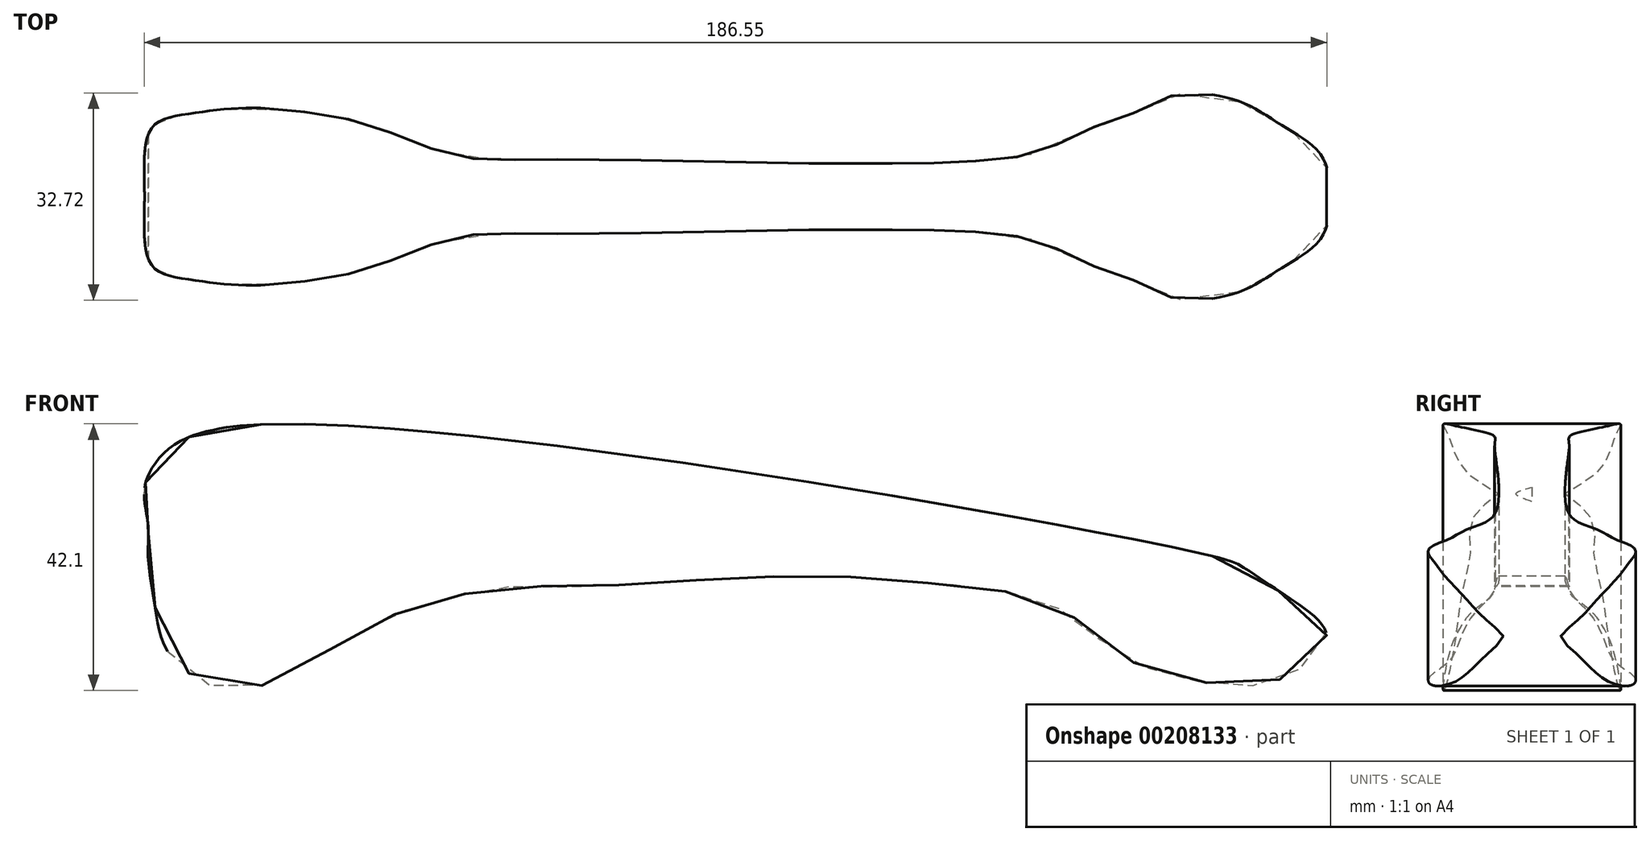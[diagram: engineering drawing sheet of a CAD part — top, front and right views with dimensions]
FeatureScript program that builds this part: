
annotation { "Feature Type Name" : "Feature", "Feature Type Description" : "" }
export const myFeature = defineFeature(function(context is Context, id is Id, definition is map)
    precondition{}
    {
        {
            var Q0;
            Q0=qCreatedBy(makeId("Front.planeOp"),FACE);
            var sketch = newSketch(context, id + "F0", { "sketchPlane" : qUnion([Q0])});
            skFitSpline(sketch, "E0", {"points": [v(-91, 27.57) * mm, v(-74.43, 33.6) * mm, v(75.64, 12.8) * mm, v(81.06, 10.7) * mm, v(88.3, 5.88) * mm, v(93.72, 0) * mm, v(88.6, -5.58) * mm, v(80.46, -7.68) * mm, v(68.7, -5.88) * mm, v(60.27, -2.26) * mm, v(53.34, 3.47) * mm, v(40.68, 7.68) * mm, v(30.14, 8.59) * mm, v(19.29, 9.5) * mm, v(3.31, 9.5) * mm, v(-7.53, 8.9) * mm, v(-26.22, 7.99) * mm, v(-35.56, 7.99) * mm, v(-44.9, 6.18) * mm, v(-53.64, 3.47) * mm, v(-59.97, 0) * mm, v(-68.7, -4.67) * mm, v(-74.43, -7.68) * mm, v(-81.37, -7.99) * mm, v(-88.9, -2.56) * mm, v(-91, 4.07) * mm, v(-92.21, 12.8) * mm, v(-92.21, 17.63) * mm, v(-92.82, 23.05) * mm, v(-91, 27.57) * mm]});
            skLineSegment(sketch, "E1", {"start": v(-74.43, 33.6) * mm, "end": v(75.64, 12.8) * mm});
            skSolve(sketch);
        }
        {
            var Q0;
            Q0=qCreatedBy(makeId("Top.planeOp"),FACE);
            var sketch = newSketch(context, id + "F1", { "sketchPlane" : qUnion([Q0])});
            skFitSpline(sketch, "E2", {"points": [v(-92.75, 0) * mm, v(-92.75, 6.78) * mm, v(-91.25, 11.3) * mm, v(-85.52, 13.1) * mm, v(-76.18, 14.01) * mm, v(-65.63, 13.1) * mm, v(-59.3, 11.9) * mm, v(-50.87, 8.9) * mm, v(-45.14, 6.78) * mm, v(-39.72, 5.88) * mm, v(-25.25, 5.88) * mm, v(41.95, 5.88) * mm, v(51.9, 8.59) * mm, v(57.02, 11) * mm, v(63.05, 13.1) * mm, v(69.98, 16.12) * mm, v(80.22, 14.92) * mm, v(86.55, 11.3) * mm, v(92.88, 6.48) * mm, v(94.09, 0) * mm], "startDerivative": vector(-5.23, 154.82) * mm, "endDerivative": vector(0.21, -157.7) * mm});
            skLineSegment(sketch, "E3", {"start": v(-108.43, 0) * mm, "end": v(107.95, 0) * mm});
            skFitSpline(sketch, "E4.MirrorCS", {"points": [v(-92.75, 0) * mm, v(-92.75, -6.78) * mm, v(-91.25, -11.3) * mm, v(-85.52, -13.1) * mm, v(-76.18, -14.01) * mm, v(-65.63, -13.1) * mm, v(-59.3, -11.9) * mm, v(-50.87, -8.9) * mm, v(-45.14, -6.78) * mm, v(-39.72, -5.88) * mm, v(-25.25, -5.88) * mm, v(41.95, -5.88) * mm, v(51.9, -8.59) * mm, v(57.02, -11) * mm, v(63.05, -13.1) * mm, v(69.98, -16.12) * mm, v(80.22, -14.92) * mm, v(86.55, -11.3) * mm, v(92.88, -6.48) * mm, v(94.09, 0) * mm], "startDerivative": vector(-5.23, -154.82) * mm, "endDerivative": vector(0.21, 157.7) * mm});
            skSolve(sketch);
        }
        {
            var Q0;
            Q0=qSketchRegion(id+"F0",true);
            extrude(context, id + "F2", {"entities" : qUnion([Q0]), "endBound" : BoundingType.SYMMETRIC, "depth" : 38.1 * mm});
        }
        {
            var Q0;
            Q0=qSketchRegion(id+"F1",true);
            extrude(context, id + "F3", {"entities" : qUnion([Q0]), "operationType" : NewBodyOperationType.INTERSECT, "endBound" : BoundingType.THROUGH_ALL, "depth" : 25.4 * mm, "hasSecondDirection" : true, "secondDirectionOppositeDirection" : true, "secondDirectionDepth" : 25.4 * mm});
        }
    });
